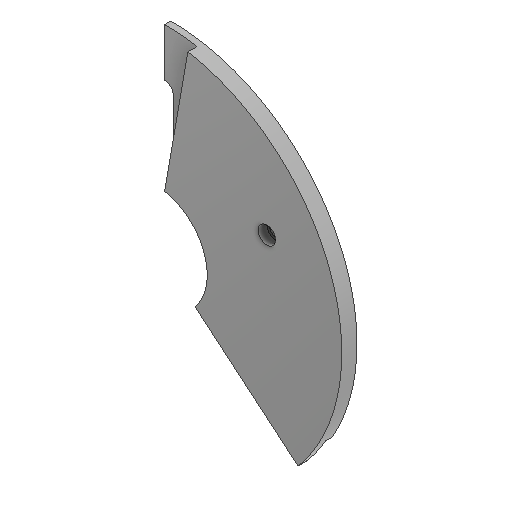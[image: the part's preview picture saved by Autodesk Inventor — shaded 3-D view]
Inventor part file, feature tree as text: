
AUTODESK INVENTOR PART (.ipt)
format: ipt  version: 2025 (Build 290162000, 162)  size: 165,888 bytes
history: native  units: mm
features: extrude x5, sketch x5, projected_geometry x4, thicken_offset x1
ambient origin geometry x8: Origin, YZ Plane, XZ Plane, XY Plane, X Axis, Y Axis, Z Axis, Center Point
bodies: Solid1 (feature_tree)
feature tree (15):
  extrude  "Extrusion1"  Depth=172.0mm
  extrude  "Extrusion2"  Depth=7.0mm TaperAngle=0.0deg
  extrude  "Extrusion3"  Depth=5.5mm
  extrude  "Extrusion4"  Depth=8.0mm
  extrude  "Extrusion5"  Depth=4.25mm
  thicken_offset  "Thicken1"
  sketch  "Sketch1"  dims[d0=48.0mm d1=172.0mm]
  sketch  "Sketch2"  dims[d2=120.0deg d3=7.0mm d4=0.0mm]
  projected_geometry  "Projected Loop1"
  sketch  "Sketch3"  dims[d5=119.0mm d6=5.5mm]
  projected_geometry  "Projected Loop2"
  sketch  "Sketch4"  dims[d7=60.0deg d8=8.0mm]
  projected_geometry  "Projected Loop3"
  sketch  "Sketch5"  dims[d9=4.0mm d10=0.0mm d11=4.25mm d12=4.25mm d13=3.0mm d14=0.0mm d15=1.745329mm d16=3.0mm d17=0.0mm d18=1.745329mm d19=10.0mm d20=0.0mm d21=0.2mm d22=0.2mm]
  projected_geometry  "Projected Loop4"
